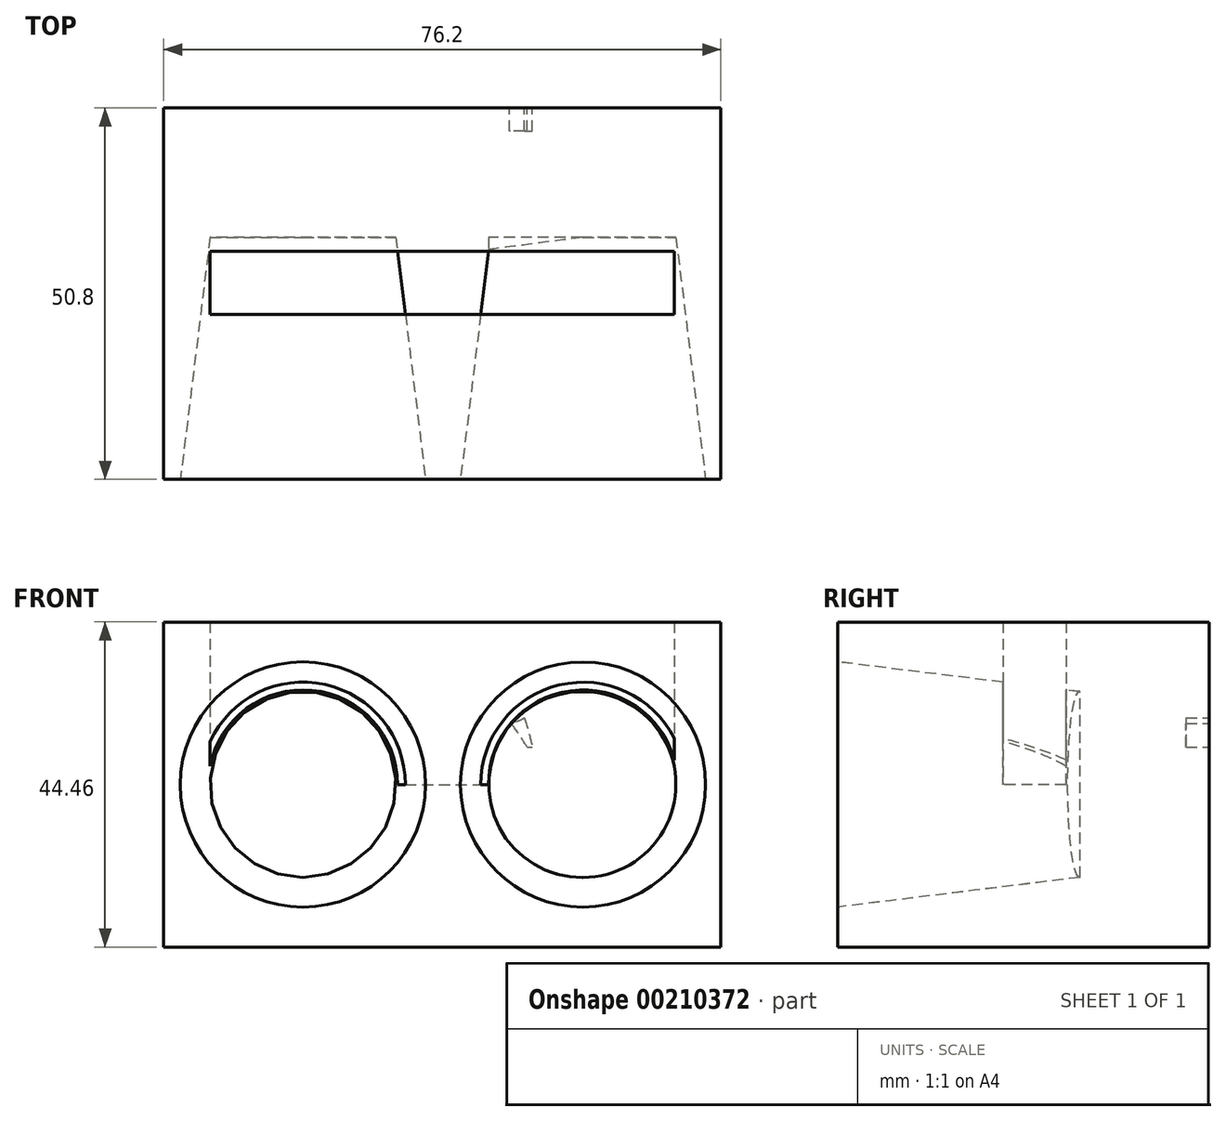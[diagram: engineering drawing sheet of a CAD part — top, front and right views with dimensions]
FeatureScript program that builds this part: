
annotation { "Feature Type Name" : "Feature", "Feature Type Description" : "" }
export const myFeature = defineFeature(function(context is Context, id is Id, definition is map)
    precondition{}
    {
        {
            var Q0;
            Q0=qCreatedBy(makeId("Front.planeOp"),FACE);
            var sketch = newSketch(context, id + "F0", { "sketchPlane" : qUnion([Q0])});
            skLineSegment(sketch, "E0.bottom", {"start": v(38.1, 22.23) * mm, "end": v(-38.1, 22.22) * mm});
            skLineSegment(sketch, "E0.top", {"start": v(38.1, -22.22) * mm, "end": v(-38.1, -22.23) * mm});
            skLineSegment(sketch, "E0.left", {"start": v(38.1, 22.23) * mm, "end": v(38.1, -22.22) * mm});
            skLineSegment(sketch, "E0.right", {"start": v(-38.1, 22.22) * mm, "end": v(-38.1, -22.23) * mm});
            skSolve(sketch);
        }
        {
            var Q0;
            Q0=qSketchRegion(id+"F0",true);
            extrude(context, id + "F1", {"entities" : qUnion([Q0]), "depth" : 50.8 * mm});
        }
        {
            var Q0;
            Q0=qCreatedBy(makeId("Top.planeOp"),FACE);
            var sketch = newSketch(context, id + "F2", { "sketchPlane" : qUnion([Q0])});
            skLineSegment(sketch, "E1.top", {"start": v(0.69, -28.24) * mm, "end": v(31.75, -28.24) * mm});
            skLineSegment(sketch, "E2.bottom", {"start": v(31.75, -28.24) * mm, "end": v(-31.75, -28.24) * mm});
            skLineSegment(sketch, "E2.top", {"start": v(31.75, -19.6) * mm, "end": v(-31.75, -19.6) * mm});
            skLineSegment(sketch, "E2.left", {"start": v(31.75, -28.24) * mm, "end": v(31.75, -19.6) * mm});
            skLineSegment(sketch, "E2.right", {"start": v(-31.75, -28.24) * mm, "end": v(-31.75, -19.6) * mm});
            skSolve(sketch);
        }
        {
            var Q0;
            Q0=qSketchRegion(id+"F2",true);
            extrude(context, id + "F3", {"entities" : qUnion([Q0]), "operationType" : NewBodyOperationType.REMOVE, "depth" : 34.24 * mm});
        }
        {
            var Q0;
            Q0=makeQuery(id+"F1.opExtrude","CAP_FACE",FACE,{"disambiguationData":[OSD([sQuery(id+"F0.wireOp",EDGE,"E0.bottom"),sQuery(id+"F0.wireOp",EDGE,"E0.top"),sQuery(id+"F0.wireOp",EDGE,"E0.left"),sQuery(id+"F0.wireOp",EDGE,"E0.right")])],"isStart":false});
            var sketch = newSketch(context, id + "F4", { "sketchPlane" : qUnion([Q0])});
            skCircle(sketch, "E3", {"center": v(-19.05, 0) * mm, "radius": 12.7 * mm});
            skCircle(sketch, "E4", {"center": v(19.05, 0) * mm, "radius": 12.7 * mm});
            skSolve(sketch);
        }
        {
            var Q0;
            Q0=makeQuery(id+"F4.imprint","IMPRINT",FACE,{"disambiguationData":[TD([[makeQuery(id+"F4.imprint","IMPRINT",EDGE,{"derivedFrom":sQuery(id+"F4.wireOp",EDGE,"E4")}),1.0]])]});
            var Q1;
            Q1=makeQuery(id+"F4.imprint","IMPRINT",FACE,{"disambiguationData":[TD([[makeQuery(id+"F4.imprint","IMPRINT",EDGE,{"derivedFrom":sQuery(id+"F4.wireOp",EDGE,"E3")}),1.0]])]});
            extrude(context, id + "F5", {"entities" : qUnion([Q0, Q1]), "operationType" : NewBodyOperationType.REMOVE, "oppositeDirection" : true, "depth" : 33.1 * mm});
        }
        {
            var Q0;
            Q0=makeQuery(id+"F5.boolean.opBoolean","COPY",FACE,{"derivedFrom":makeQuery(id+"F5.opExtrude","CAP_FACE",FACE,{"disambiguationData":[OSD([sQuery(id+"F4.wireOp",EDGE,"E3")])],"isStart":false})});
            var sketch = newSketch(context, id + "F6", { "sketchPlane" : qUnion([Q0])});
            skCircle(sketch, "E5", {"center": v(-19.05, 0) * mm, "radius": 12.7 * mm});
            skCircle(sketch, "E6", {"center": v(19.25, 0) * mm, "radius": 12.7 * mm});
            skSolve(sketch);
        }
        {
            var Q0;
            Q0=qSketchRegion(id+"F6",true);
            extrude(context, id + "F7", {"entities" : qUnion([Q0]), "operationType" : NewBodyOperationType.REMOVE, "depth" : 47.6 * mm, "hasDraft" : true, "draftAngle" : 7 * degree});
        }
        {
            var Q0;
            Q0=makeQuery(id+"F1.opExtrude","CAP_FACE",FACE,{"disambiguationData":[OSD([sQuery(id+"F0.wireOp",EDGE,"E0.bottom"),sQuery(id+"F0.wireOp",EDGE,"E0.top"),sQuery(id+"F0.wireOp",EDGE,"E0.left"),sQuery(id+"F0.wireOp",EDGE,"E0.right")])],"isStart":true});
            var sketch = newSketch(context, id + "F8", { "sketchPlane" : qUnion([Q0])});
            skFitSpline(sketch, "E7.MirrorCS", {"points": [v(-11.63, 5.1) * mm, v(-10.85, 6.3) * mm, v(-9.83, 7.8) * mm, v(-8.78, 8.64) * mm, v(-7, 9.26) * mm, v(-5.45, 9.42) * mm, v(-3.43, 9.42) * mm], "startDerivative": vector(4.9, 7.38) * mm, "endDerivative": vector(11.48, -0.12) * mm});
            skLineSegment(sketch, "E8.MirrorCS", {"start": v(0.06, 13.95) * mm, "end": v(9.8, 13.95) * mm});
            skPoint(sketch, "E9.MirrorP", {"position": v(-3.43, 7.35) * mm});
            skPoint(sketch, "E10.MirrorP", {"position": v(9.8, 13.95) * mm});
            skPoint(sketch, "E11.MirrorP", {"position": v(15.97, -7.75) * mm});
            skPoint(sketch, "E12.MirrorP", {"position": v(-9.64, 11.94) * mm});
            skLineSegment(sketch, "E13.MirrorCS", {"start": v(6.22, 9.55) * mm, "end": v(-0.6, 9.47) * mm});
            skFitSpline(sketch, "E14.MirrorCS", {"points": [v(-3.43, 9.42) * mm, v(-3.43, 7.35) * mm, v(-3.8, 3.63) * mm, v(-4.81, -1.09) * mm, v(-6.21, -4.45) * mm, v(-7.66, -7.06) * mm, v(-9.06, -8.8) * mm, v(-10.33, -11.15) * mm, v(-9.83, -13.81) * mm, v(-8, -14.9) * mm, v(-5.45, -14.9) * mm, v(-3.67, -13.15) * mm, v(-2.34, -9.82) * mm, v(-1.01, 1.65) * mm, v(-0.6, 9.47) * mm], "startDerivative": vector(0.85, -35.93) * mm, "endDerivative": vector(2.87, 67.34) * mm});
            skLineSegment(sketch, "E15.MirrorCS", {"start": v(17.36, 13.92) * mm, "end": v(9.8, 13.95) * mm});
            skPoint(sketch, "E16.MirrorP", {"position": v(8.55, -14.98) * mm});
            skPoint(sketch, "E17.MirrorP", {"position": v(9.97, 4.46) * mm});
            skPoint(sketch, "E18.MirrorP", {"position": v(10.2, 9.31) * mm});
            skPoint(sketch, "E19.MirrorP", {"position": v(17.36, 13.92) * mm});
            skPoint(sketch, "E20.MirrorP", {"position": v(4.73, -11.15) * mm});
            skFitSpline(sketch, "E21.MirrorCS", {"points": [v(51.46, -8.36) * mm, v(17.23, -8.42) * mm, v(16.3, -11.16) * mm, v(14.68, -13.58) * mm, v(12.26, -14.98) * mm, v(8.55, -14.98) * mm, v(6.3, -13.65) * mm, v(4.73, -11.15) * mm, v(4.73, -7.41) * mm, v(6.22, 9.55) * mm], "startDerivative": vector(-0.66, -24.41) * mm, "endDerivative": vector(7.27, 86.48) * mm});
            skPoint(sketch, "E22.MirrorP", {"position": v(17.4, 9.31) * mm});
            skFitSpline(sketch, "E23.MirrorCS", {"points": [v(0.06, 13.95) * mm, v(-4.06, 13.77) * mm, v(-6.97, 13.3) * mm, v(-8.65, 12.67) * mm, v(-9.64, 11.94) * mm, v(-10.4, 10.94) * mm, v(-11.24, 9.1) * mm, v(22.03, 5) * mm, v(21.27, 3.19) * mm], "startDerivative": vector(-24.43, -0.6) * mm, "endDerivative": vector(-6.44, -14.63) * mm});
            skPoint(sketch, "E24.MirrorP", {"position": v(12.5, -10.27) * mm});
            skLineSegment(sketch, "E25.MirrorCS", {"start": v(17.36, 13.92) * mm, "end": v(17.4, 9.31) * mm});
            skLineSegment(sketch, "E26.MirrorCS", {"start": v(10.2, 9.31) * mm, "end": v(9.97, 4.46) * mm});
            skPoint(sketch, "E27.MirrorP", {"position": v(15.16, -9.26) * mm});
            skPoint(sketch, "E28.MirrorP", {"position": v(10.27, -9.01) * mm});
            skPoint(sketch, "E29.MirrorP", {"position": v(16.28, -6.42) * mm});
            skPoint(sketch, "E30.MirrorP", {"position": v(9.4, -6.28) * mm});
            skPoint(sketch, "E31.MirrorP", {"position": v(13.94, -10.06) * mm});
            skPoint(sketch, "E32.MirrorP", {"position": v(17.4, -6.39) * mm});
            skFitSpline(sketch, "E33.MirrorCS", {"points": [v(16.28, -6.42) * mm, v(15.97, -7.75) * mm, v(15.16, -9.26) * mm, v(13.94, -10.06) * mm, v(12.5, -10.27) * mm, v(10.27, -9.01) * mm, v(9.4, -6.28) * mm, v(9.97, 4.46) * mm], "startDerivative": vector(-2.38, -12.66) * mm, "endDerivative": vector(3.7, 43.54) * mm});
            skLineSegment(sketch, "E34.MirrorCS", {"start": v(17.4, 9.31) * mm, "end": v(10.2, 9.31) * mm});
            skFitSpline(sketch, "E35", {"points": [v(-8.65, 12.67) * mm, v(-9.64, 11.94) * mm, v(-10.4, 10.94) * mm, v(-11.24, 9.1) * mm, v(-12.3, 5.12) * mm, v(-12.3, 5.07) * mm], "startDerivative": vector(-5.58, -3.56) * mm, "endDerivative": vector(0.18, -0.68) * mm});
            skFitSpline(sketch, "E36", {"points": [v(-11.63, 5.1) * mm, v(-12.3, 5.12) * mm], "startDerivative": vector(-0.68, 0.02) * mm, "endDerivative": vector(-0.68, 0.02) * mm});
            skFitSpline(sketch, "E37", {"points": [v(16.3, -11.16) * mm, v(17.23, -8.42) * mm, v(17.4, -6.39) * mm], "startDerivative": vector(2.08, 5.2) * mm, "endDerivative": vector(0.08, 4.31) * mm});
            skFitSpline(sketch, "E38", {"points": [v(16.28, -6.42) * mm, v(17.4, -6.39) * mm], "startDerivative": vector(1.12, 0.03) * mm, "endDerivative": vector(1.12, 0.03) * mm});
            skSolve(sketch);
        }
        {
            var Q0;
            Q0=makeQuery(id+"F8.imprint","IMPRINT",FACE,{"disambiguationData":[TD([[makeQuery(id+"F8.imprint","IMPRINT",EDGE,{"derivedFrom":sQuery(id+"F8.wireOp",EDGE,"E7.MirrorCS")}),1.0]])]});
            extrude(context, id + "F9", {"entities" : qUnion([Q0]), "operationType" : NewBodyOperationType.REMOVE, "oppositeDirection" : true, "depth" : 3.17 * mm});
        }
    });
